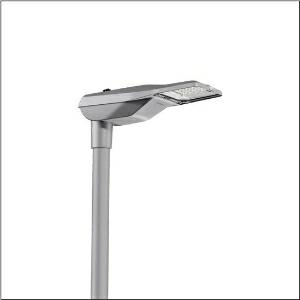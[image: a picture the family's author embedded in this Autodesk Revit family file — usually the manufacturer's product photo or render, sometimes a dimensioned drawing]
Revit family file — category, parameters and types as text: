
# Revit family: streetlight_sl_21_micro___st1_0a_5xe1d33s08db_38a0
name_source: partatom
category: Lighting Fixtures
units: mm (PartAtom-declared; Revit-internal decimal feet)

## family parameters
Cut with Voids When Loaded = No
Host = Face
Light Source = No
Part Type = Normal
Room Calculation Point = No
Round Connector Dimension = Use Diameter
Shared = No

## types (1)
- --- (1 x LED, 5110 lm, 39.1 W, 3000K)
    Apparent Load = 39 VA
    CIE Flux Codes = 37 72 97 100 100
    Color Rendering = 70
    Color Temperature = 3000K
    Default Elevation = 1800 mm
    Description = Streetlight SL 21 micro, mast luminaire, primary light control with lens, of PMMA, primary optical cover: cover, of toughened safety glass, transparent, light distribution: ST1.0a, light emission: direct distribution, primary light characteristic: asymmetric, installation type: side-entry, post-top, LED, High Power LED, rated luminous flux: 5.110lm, luminous efficacy: 131lm/W, light colour: 730, colour temperature: 3000K, control gear: D4i, control: flexible luminous flux parameterisation, time-dependent luminous flux control, constant luminous flux control, overheat protection, pre-setting: logarithmic dimming characteristic, mains connection: 220..240V, AC, 50/60Hz, start of lifetime: 39W, end of service life: 41W, reduction: 18W, luminaire housing, of diecast aluminium, powder-coated, Siteco® metallic grey (DB 702S), corrosivity category C5 mid according to DIN EN ISO 12944, please order mast flange separately, inclination adjustable: 0°, 5°, 10°, 15°, sealing non-destructively replaceable, multi-level sealing system, length: 528mm, width: 235mm, height: 110mm, mast flange for spigot size: 42mm (side-entry): 5XC10008XM4, 60/48mm (side-entry/post-top): 5XC10108XM2, 76/60mm (side-entry/post-top): 5XC10108XM1, Smart Interface above, protection rating (complete): IP66, insulation class (complete): insulation class II (safety insulation), certification: CE, ENEC, ENEC+, VDE, impact resistance: IK10, permissible operating ambient temperature for outdoor applications: -40..+50°C, standard-compliant lighting for roads and squares, packaging unit: 1 piece

Light Distribution: ST1.0a
    Height = 110 mm
    Lamp = 1 x LED
    Lamp Light Flux = 5110 lm
    Lamp Power = 39.1 W
    Lamp count = 1
    Length = 528 mm
    Luminous efficacy = 131 lm/W
    Manufacturer = Siteco
    ModVariant = No
    Model = 5XE1D33S08DB
    Number of Poles = 1
    OnlyDefault = Yes
    Power Factor = 1
    Product Name = Streetlight SL 21 micro | ST1.0a
    Product group = mast luminaire | pylon top
    ProductGroupID = 6100
    Protection Class = Protection class II
    Protection Degree = IP 66
    RLX_Detail_Level = 1
    RLX_Emergency_Light_Flux = 0 lm
    RLX_Emergency_Type = 0
    RLX_Emergency_Type_DB = No
    RlxData = <blob elided: 98977 chars, md5=af6e1d8b>
    Socket = socket
    Standby Power = 0 W
    System Light Flux = 5110 lm
    System Power = 39 W
    Type Comments = factory setting: luminous flux: 100 % | dim-lin: 254 | 765 mA
    Type Image = l_1277292.jpg
    URL = http://relux.com
    VarID = @adj_177315
    Voltage = 0 V
    Weight = 0.00 kg
    Width = 235 mm

## geometry (parser evidence)
native form markers: Blend x4, Sweep x10
no freeform markers — native parametric forms only
